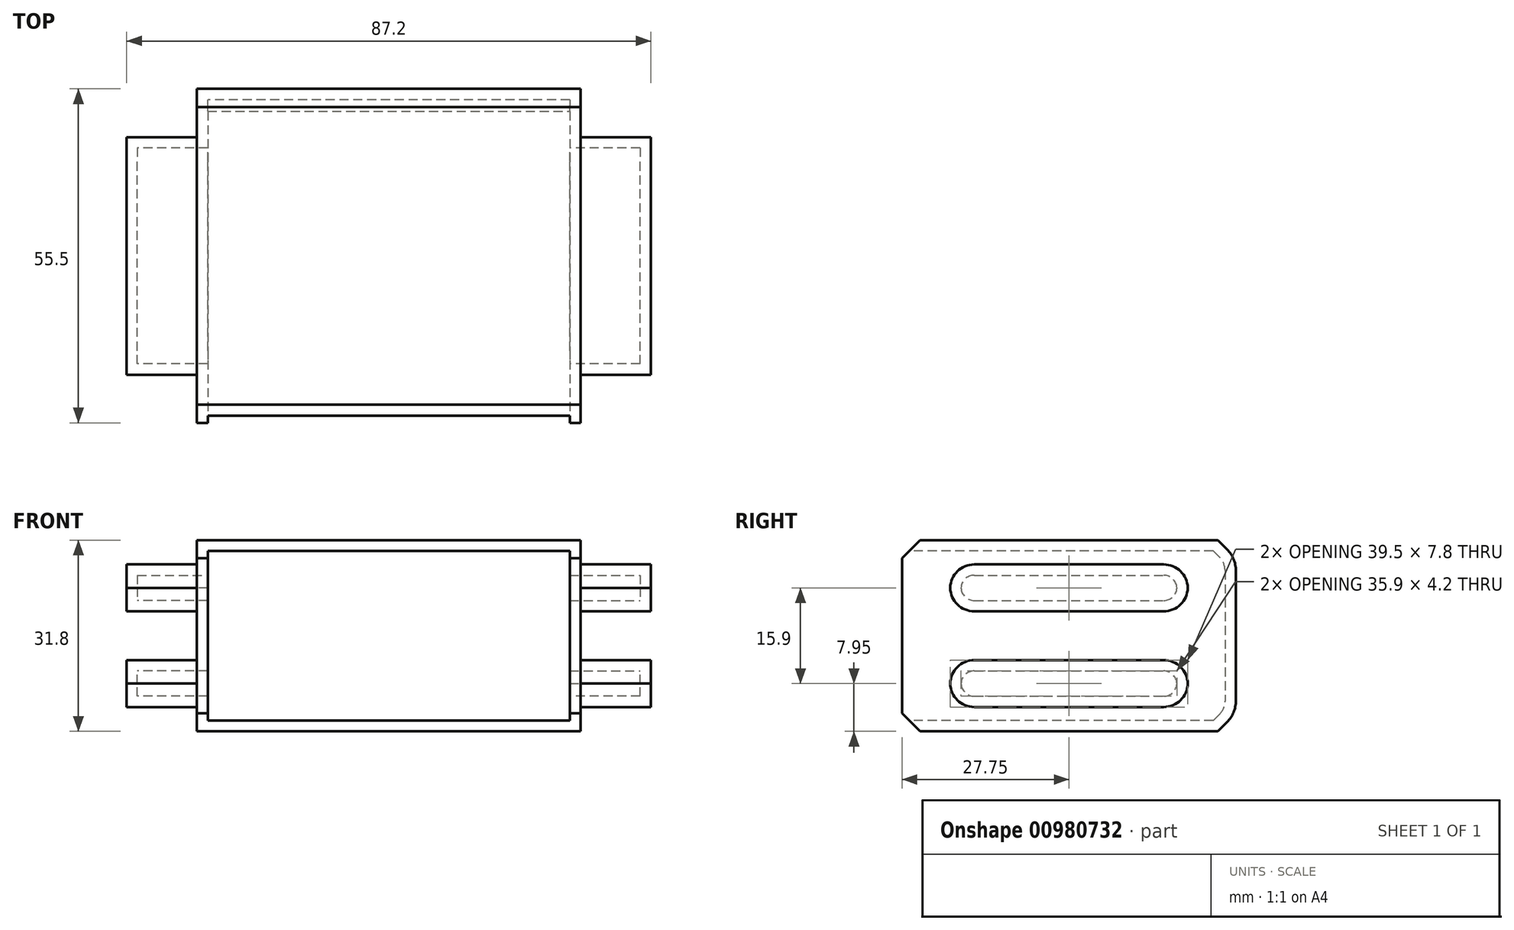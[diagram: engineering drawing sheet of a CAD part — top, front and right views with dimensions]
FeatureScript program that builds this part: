
annotation { "Feature Type Name" : "Feature", "Feature Type Description" : "" }
export const myFeature = defineFeature(function(context is Context, id is Id, definition is map)
    precondition{}
    {
        {
            assignVariable(context, id + "F0", {"name" : "Wallthickness", "anyValue" : 1.8});
        }
        {
            var Q0;
            Q0=qCreatedBy(makeId("Top.planeOp"),FACE);
            var sketch = newSketch(context, id + "F1", { "sketchPlane" : qUnion([Q0])});
            skLineSegment(sketch, "E0", {"start": v(0, 27.75) * mm, "end": v(31.9, 27.75) * mm});
            skLineSegment(sketch, "E1", {"start": v(31.9, 27.75) * mm, "end": v(31.9, 0) * mm});
            skLineSegment(sketch, "E2.MirrorCS", {"start": v(0, -27.75) * mm, "end": v(31.9, -27.75) * mm});
            skLineSegment(sketch, "E3.MirrorCS", {"start": v(31.9, -27.75) * mm, "end": v(31.9, 0) * mm});
            skLineSegment(sketch, "E4", {"start": v(0, 27.75) * mm, "end": v(0, -27.75) * mm});
            skSolve(sketch);
        }
        {
            var Q0;
            Q0=makeQuery(id+"F1.imprint","IMPRINT",FACE,{"disambiguationData":[TD([[makeQuery(id+"F1.imprint","IMPRINT",EDGE,{"derivedFrom":sQuery(id+"F1.wireOp",EDGE,"E0")}),-1.0]])]});
            extrude(context, id + "F2", {"entities" : qUnion([Q0]), "depth" : 15.9 * mm, "offsetDistance" : 25 * mm});
        }
        {
            var Q0;
            Q0=makeQuery(id+"F8.opPattern","COPY",EDGE,{"derivedFrom":makeQuery(id+"F2.opExtrude","CAP_EDGE",EDGE,{"disambiguationData":[OSD([sQuery(id+"F1.wireOp",EDGE,"E0"),sQuery(id+"F1.wireOp",EDGE,"d8e08b7d-7ed0-4e81-b9dd-cc205c2170ec0.MirrorCS")])],"isStart":false}),"instanceName":"1"});
            var Q1;
            Q1=makeQuery(id+"F2.opExtrude","CAP_EDGE",EDGE,{"disambiguationData":[OSD([sQuery(id+"F1.wireOp",EDGE,"E0"),sQuery(id+"F1.wireOp",EDGE,"d8e08b7d-7ed0-4e81-b9dd-cc205c2170ec0.MirrorCS")])],"isStart":false});
            chamfer(context, id + "F3", {"entities" : qUnion([Q0, Q1]), "width" : 3 * mm, "tangentPropagation" : true});
        }
        {
            var Q0;
            {var subQ0=sQuery(id+"F1.wireOp",EDGE,"dba99d8c-e612-43e0-9807-e2244816e7270.MirrorCS");var subQ1=sQuery(id+"F1.wireOp",EDGE,"E2.MirrorCS");var subQ2=makeQuery(id+"F2.opExtrude","SWEPT_FACE",FACE,{"disambiguationData":[OSD([subQ1,subQ0])]});Q0=makeQuery(id+"F3.opChamfer","BLEND_EDGE",EDGE,{"blendedFrom":[makeQuery(id+"F2.opExtrude","CAP_EDGE",EDGE,{"disambiguationData":[OSD([subQ1,subQ0])],"isStart":false}),makeQuery(id+"F8.boolean.opBoolean","MERGE",FACE,{"derivedFrom":[subQ2,makeQuery(id+"F8.opPattern","COPY",FACE,{"derivedFrom":subQ2,"instanceName":"1"})]})],"blendedInto":[makeQuery(id+"F8.boolean.opBoolean","MERGE",FACE,{"derivedFrom":[subQ2,makeQuery(id+"F8.opPattern","COPY",FACE,{"derivedFrom":subQ2,"instanceName":"1"})]})]});}
            var Q1;
            {var subQ0=sQuery(id+"F1.wireOp",EDGE,"dba99d8c-e612-43e0-9807-e2244816e7270.MirrorCS");var subQ1=sQuery(id+"F1.wireOp",EDGE,"E2.MirrorCS");var subQ2=makeQuery(id+"F2.opExtrude","SWEPT_FACE",FACE,{"disambiguationData":[OSD([subQ1,subQ0])]});Q1=makeQuery(id+"F3.opChamfer","BLEND_EDGE",EDGE,{"blendedFrom":[makeQuery(id+"F8.opPattern","COPY",EDGE,{"derivedFrom":makeQuery(id+"F2.opExtrude","CAP_EDGE",EDGE,{"disambiguationData":[OSD([subQ1,subQ0])],"isStart":false}),"instanceName":"1"}),makeQuery(id+"F8.boolean.opBoolean","MERGE",FACE,{"derivedFrom":[subQ2,makeQuery(id+"F8.opPattern","COPY",FACE,{"derivedFrom":subQ2,"instanceName":"1"})]})],"blendedInto":[makeQuery(id+"F8.boolean.opBoolean","MERGE",FACE,{"derivedFrom":[subQ2,makeQuery(id+"F8.opPattern","COPY",FACE,{"derivedFrom":subQ2,"instanceName":"1"})]})]});}
            var Q2;
            {var subQ0=sQuery(id+"F1.wireOp",EDGE,"d8e08b7d-7ed0-4e81-b9dd-cc205c2170ec0.MirrorCS");var subQ1=sQuery(id+"F1.wireOp",EDGE,"E0");var subQ2=makeQuery(id+"F2.opExtrude","SWEPT_FACE",FACE,{"disambiguationData":[OSD([subQ1,subQ0])]});Q2=makeQuery(id+"F3.opChamfer","BLEND_EDGE",EDGE,{"blendedFrom":[makeQuery(id+"F8.opPattern","COPY",EDGE,{"derivedFrom":makeQuery(id+"F2.opExtrude","CAP_EDGE",EDGE,{"disambiguationData":[OSD([subQ1,subQ0])],"isStart":false}),"instanceName":"1"}),makeQuery(id+"F8.boolean.opBoolean","MERGE",FACE,{"derivedFrom":[subQ2,makeQuery(id+"F8.opPattern","COPY",FACE,{"derivedFrom":subQ2,"instanceName":"1"})]})],"blendedInto":[makeQuery(id+"F8.boolean.opBoolean","MERGE",FACE,{"derivedFrom":[subQ2,makeQuery(id+"F8.opPattern","COPY",FACE,{"derivedFrom":subQ2,"instanceName":"1"})]})]});}
            var Q3;
            {var subQ0=sQuery(id+"F1.wireOp",EDGE,"d8e08b7d-7ed0-4e81-b9dd-cc205c2170ec0.MirrorCS");var subQ1=sQuery(id+"F1.wireOp",EDGE,"E0");var subQ2=makeQuery(id+"F2.opExtrude","SWEPT_FACE",FACE,{"disambiguationData":[OSD([subQ1,subQ0])]});Q3=makeQuery(id+"F3.opChamfer","BLEND_EDGE",EDGE,{"blendedFrom":[makeQuery(id+"F2.opExtrude","CAP_EDGE",EDGE,{"disambiguationData":[OSD([subQ1,subQ0])],"isStart":false}),makeQuery(id+"F8.boolean.opBoolean","MERGE",FACE,{"derivedFrom":[subQ2,makeQuery(id+"F8.opPattern","COPY",FACE,{"derivedFrom":subQ2,"instanceName":"1"})]})],"blendedInto":[makeQuery(id+"F8.boolean.opBoolean","MERGE",FACE,{"derivedFrom":[subQ2,makeQuery(id+"F8.opPattern","COPY",FACE,{"derivedFrom":subQ2,"instanceName":"1"})]})]});}
            fillet(context, id + "F4", {"entities" : qUnion([Q0, Q1, Q2, Q3]), "radius" : 5 * mm, "tangentPropagation" : true, "allowEdgeOverflow" : false});
        }
        {
            var Q0;
            {var subQ0=makeQuery(id+"F2.opExtrude","SWEPT_FACE",FACE,{"disambiguationData":[OSD([sQuery(id+"F1.wireOp",EDGE,"E1"),sQuery(id+"F1.wireOp",EDGE,"E3.MirrorCS")])]});Q0=makeQuery(id+"F8.boolean.opBoolean","MERGE",FACE,{"derivedFrom":[subQ0,makeQuery(id+"F8.opPattern","COPY",FACE,{"derivedFrom":subQ0,"instanceName":"1"})]});}
            var sketch = newSketch(context, id + "F5", { "sketchPlane" : qUnion([Q0])});
            skLineSegment(sketch, "E5.bottom", {"start": v(-19.75, 11.85) * mm, "end": v(0, 11.85) * mm});
            skLineSegment(sketch, "E5.top", {"start": v(-19.75, 4.05) * mm, "end": v(0, 4.05) * mm});
            skLineSegment(sketch, "E5.left", {"start": v(-19.75, 11.85) * mm, "end": v(-19.75, 4.05) * mm});
            skLineSegment(sketch, "E6.MirrorCS", {"start": v(19.75, 11.85) * mm, "end": v(0, 11.85) * mm});
            skLineSegment(sketch, "E7.MirrorCS", {"start": v(19.75, 11.85) * mm, "end": v(19.75, 4.05) * mm});
            skLineSegment(sketch, "E8.MirrorCS", {"start": v(19.75, 4.05) * mm, "end": v(0, 4.05) * mm});
            skSolve(sketch);
        }
        {
            var Q0;
            Q0 = qSketchRegion(id + "F5", true);
            extrude(context, id + "F6", {"entities" : qUnion([Q0]), "operationType" : NewBodyOperationType.ADD, "depth" : 11.7 * mm, "offsetDistance" : 25 * mm});
        }
        {
            var Q0;
            Q0=makeQuery(id+"F6.opExtrude","SWEPT_EDGE",EDGE,{"disambiguationData":[OSD([sQuery(id+"F5.wireOp",EDGE,"E5.top"),sQuery(id+"F5.wireOp",EDGE,"E5.left")])]});
            var Q1;
            Q1=makeQuery(id+"F6.opExtrude","SWEPT_EDGE",EDGE,{"disambiguationData":[OSD([sQuery(id+"F5.wireOp",EDGE,"E5.bottom"),sQuery(id+"F5.wireOp",EDGE,"E5.left")])]});
            var Q2;
            Q2=makeQuery(id+"F6.opExtrude","SWEPT_EDGE",EDGE,{"disambiguationData":[OSD([sQuery(id+"F5.wireOp",EDGE,"E6.MirrorCS"),sQuery(id+"F5.wireOp",EDGE,"E7.MirrorCS")])]});
            var Q3;
            Q3=makeQuery(id+"F6.opExtrude","SWEPT_EDGE",EDGE,{"disambiguationData":[OSD([sQuery(id+"F5.wireOp",EDGE,"E7.MirrorCS"),sQuery(id+"F5.wireOp",EDGE,"E8.MirrorCS")])]});
            fillet(context, id + "F7", {"entities" : qUnion([Q0, Q1, Q2, Q3]), "radius" : 4 * mm, "tangentPropagation" : true, "allowEdgeOverflow" : false});
        }
        {
            var Q0;
            Q0=makeQuery(id+"F2.opExtrude","SWEPT_BODY",BODY,{"disambiguationData":[OSD([sQuery(id+"F1.wireOp",EDGE,"E0"),sQuery(id+"F1.wireOp",EDGE,"E1"),sQuery(id+"F1.wireOp",EDGE,"d8e08b7d-7ed0-4e81-b9dd-cc205c2170ec0.MirrorCS"),sQuery(id+"F1.wireOp",EDGE,"41afdc7d-a11a-4a76-b64b-28b18db2bd750.MirrorCS"),sQuery(id+"F1.wireOp",EDGE,"E2.MirrorCS"),sQuery(id+"F1.wireOp",EDGE,"E3.MirrorCS"),sQuery(id+"F1.wireOp",EDGE,"dba99d8c-e612-43e0-9807-e2244816e7270.MirrorCS"),sQuery(id+"F1.wireOp",EDGE,"6612d967-ed4d-4f94-a731-8811f257db4c0.MirrorCS")])]});
            var Q1;
            Q1=qCreatedBy(makeId("Top.planeOp"),FACE);
            mirror(context, id + "F8", {"operationType" : NewBodyOperationType.ADD, "entities" : qUnion([Q0]), "mirrorPlane" : qUnion([Q1])});
        }
        {
            var Q0;
            Q0=makeQuery(id+"F2.opExtrude","SWEPT_BODY",BODY,{"disambiguationData":[OSD([sQuery(id+"F1.wireOp",EDGE,"E0"),sQuery(id+"F1.wireOp",EDGE,"E1"),sQuery(id+"F1.wireOp",EDGE,"d8e08b7d-7ed0-4e81-b9dd-cc205c2170ec0.MirrorCS"),sQuery(id+"F1.wireOp",EDGE,"41afdc7d-a11a-4a76-b64b-28b18db2bd750.MirrorCS"),sQuery(id+"F1.wireOp",EDGE,"E2.MirrorCS"),sQuery(id+"F1.wireOp",EDGE,"E3.MirrorCS"),sQuery(id+"F1.wireOp",EDGE,"dba99d8c-e612-43e0-9807-e2244816e7270.MirrorCS"),sQuery(id+"F1.wireOp",EDGE,"6612d967-ed4d-4f94-a731-8811f257db4c0.MirrorCS")])]});
            var Q1;
            Q1=qCreatedBy(makeId("Right.planeOp"),FACE);
            mirror(context, id + "F9", {"operationType" : NewBodyOperationType.ADD, "entities" : qUnion([Q0]), "mirrorPlane" : qUnion([Q1])});
        }
        {
            var Q0;
            {var subQ0=makeQuery(id+"F2.opExtrude","SWEPT_FACE",FACE,{"disambiguationData":[OSD([sQuery(id+"F1.wireOp",EDGE,"E2.MirrorCS")])]});var subQ1=makeQuery(id+"F8.boolean.opBoolean","MERGE",FACE,{"derivedFrom":[subQ0,makeQuery(id+"F8.opPattern","COPY",FACE,{"derivedFrom":subQ0,"instanceName":"1"})]});Q0=makeQuery(id+"F9.boolean.opBoolean","MERGE",FACE,{"derivedFrom":[subQ1,makeQuery(id+"F9.opPattern","COPY",FACE,{"derivedFrom":subQ1,"instanceName":"1"})]});}
            shell(context, id + "F10", {"entities" : qUnion([Q0]), "thickness" : (getVariable(context, 'Wallthickness')) * mm});
        }
        {
            var Q0;
            Q0=makeQuery(id+"F2.opExtrude","CAP_EDGE",EDGE,{"disambiguationData":[OSD([sQuery(id+"F1.wireOp",EDGE,"E2.MirrorCS"),sQuery(id+"F1.wireOp",EDGE,"dba99d8c-e612-43e0-9807-e2244816e7270.MirrorCS")])],"isStart":false});
            var Q1;
            Q1=makeQuery(id+"F8.opPattern","COPY",EDGE,{"derivedFrom":makeQuery(id+"F2.opExtrude","CAP_EDGE",EDGE,{"disambiguationData":[OSD([sQuery(id+"F1.wireOp",EDGE,"E2.MirrorCS"),sQuery(id+"F1.wireOp",EDGE,"dba99d8c-e612-43e0-9807-e2244816e7270.MirrorCS")])],"isStart":false}),"instanceName":"1"});
            chamfer(context, id + "F11", {"entities" : qUnion([Q0, Q1]), "width" : 3 * mm, "tangentPropagation" : true});
        }
    });
